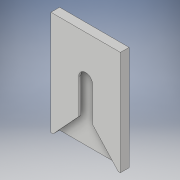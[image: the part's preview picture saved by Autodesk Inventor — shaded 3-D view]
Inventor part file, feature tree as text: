
AUTODESK INVENTOR PART (.ipt)
format: ipt  version: 2019 (Build 230136000, 136)  size: 126,464 bytes
history: native  units: in
note: dims shown in document units (in); Inventor stores cm internally (conversion verified against a paired STEP export)
features: extrude x3, sketch x3
ambient origin geometry x8: Origin, YZ Plane, XZ Plane, XY Plane, X Axis, Y Axis, Z Axis, Center Point
bodies: Solid1 (feature_tree)
feature tree (6):
  extrude  "Extrusion1"  Depth=3.0in
  extrude  "Extrusion2"  Depth=0.0625in
  extrude  "Extrusion3"  Depth=0.2in
  sketch  "Sketch1"  dims[d0=2.0in d1=3.0in]
  sketch  "Sketch2"  dims[d2=0.25in d3=0.0in d4=0.0625in]
  sketch  "Sketch3"  dims[d5=2.5in d6=0.0in d7=0.2in d8=0.2in d9=0.5in d10=0.2in d11=1.0in d12=1.0in d13=0.1875in d14=0.0in]
